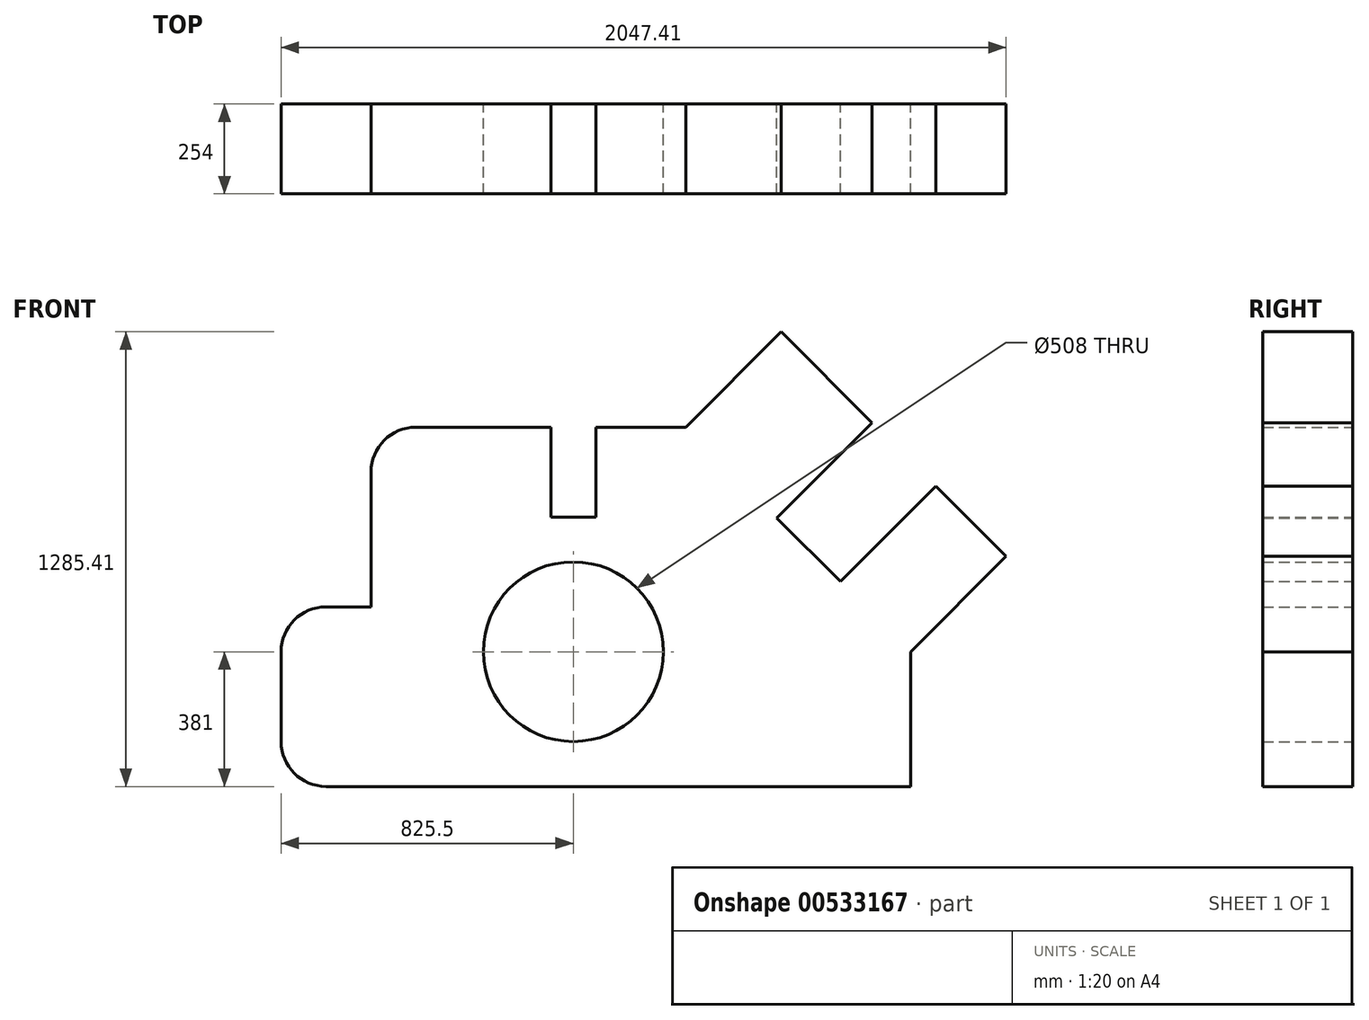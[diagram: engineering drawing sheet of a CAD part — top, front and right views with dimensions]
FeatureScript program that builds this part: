
annotation { "Feature Type Name" : "Feature", "Feature Type Description" : "" }
export const myFeature = defineFeature(function(context is Context, id is Id, definition is map)
    precondition{}
    {
        {
            var Q0;
            Q0=qCreatedBy(makeId("Front.planeOp"),FACE);
            var sketch = newSketch(context, id + "F0", { "sketchPlane" : qUnion([Q0])});
            skLineSegment(sketch, "E0", {"start": v(127, 0) * mm, "end": v(1778, 0) * mm});
            skLineSegment(sketch, "E1", {"start": v(0, 127) * mm, "end": v(0, 381) * mm});
            skPoint(sketch, "E2.visualSharp", {"position": v(0, 0) * mm});
            skArc(sketch, "E2.filletArc", {"start": v(0, 127) * mm, "mid": v(37.2, 37.2) * mm, "end": v(127, 0) * mm});
            skLineSegment(sketch, "E3", {"start": v(127, 508) * mm, "end": v(254, 508) * mm});
            skPoint(sketch, "E4.visualSharp", {"position": v(0, 508) * mm});
            skArc(sketch, "E4.filletArc", {"start": v(127, 508) * mm, "mid": v(37.2, 470.8) * mm, "end": v(0, 381) * mm});
            skLineSegment(sketch, "E5", {"start": v(254, 508) * mm, "end": v(254, 889) * mm});
            skLineSegment(sketch, "E6", {"start": v(381, 1016) * mm, "end": v(762, 1016) * mm});
            skPoint(sketch, "E7.visualSharp", {"position": v(254, 1016) * mm});
            skArc(sketch, "E7.filletArc", {"start": v(381, 1016) * mm, "mid": v(291.2, 978.8) * mm, "end": v(254, 889) * mm});
            skLineSegment(sketch, "E8", {"start": v(762, 1016) * mm, "end": v(762, 762) * mm});
            skLineSegment(sketch, "E9", {"start": v(762, 762) * mm, "end": v(889, 762) * mm});
            skLineSegment(sketch, "E10", {"start": v(889, 762) * mm, "end": v(889, 1016) * mm});
            skLineSegment(sketch, "E11", {"start": v(889, 1016) * mm, "end": v(1143, 1016) * mm});
            skLineSegment(sketch, "E12", {"start": v(1778, 0) * mm, "end": v(1778, 381) * mm});
            skLineSegment(sketch, "E13", {"start": v(1778, 381) * mm, "end": v(2047.4, 650.4) * mm});
            skLineSegment(sketch, "E14", {"start": v(2047.4, 650.4) * mm, "end": v(1849, 848.8) * mm});
            skLineSegment(sketch, "E15", {"start": v(1849, 848.8) * mm, "end": v(1579.6, 579.4) * mm});
            skLineSegment(sketch, "E16", {"start": v(1579.6, 579.4) * mm, "end": v(1400, 759) * mm});
            skLineSegment(sketch, "E17", {"start": v(1400, 759) * mm, "end": v(1669.4, 1028.41) * mm});
            skLineSegment(sketch, "E18", {"start": v(1669.4, 1028.41) * mm, "end": v(1412.4, 1285.4) * mm});
            skLineSegment(sketch, "E19", {"start": v(1412.4, 1285.4) * mm, "end": v(1143, 1016) * mm});
            skCircle(sketch, "E20", {"center": v(825.5, 381) * mm, "radius": 254 * mm});
            skSolve(sketch);
        }
        {
            var Q0;
            Q0=makeQuery(id+"F0.imprint","IMPRINT",FACE,{"disambiguationData":[TD([[makeQuery(id+"F0.imprint","IMPRINT",EDGE,{"derivedFrom":sQuery(id+"F0.wireOp",EDGE,"E0")}),1.0]])]});
            extrude(context, id + "F1", {"entities" : qUnion([Q0]), "depth" : 254 * mm, "offsetDistance" : 25.4 * mm});
        }
    });
